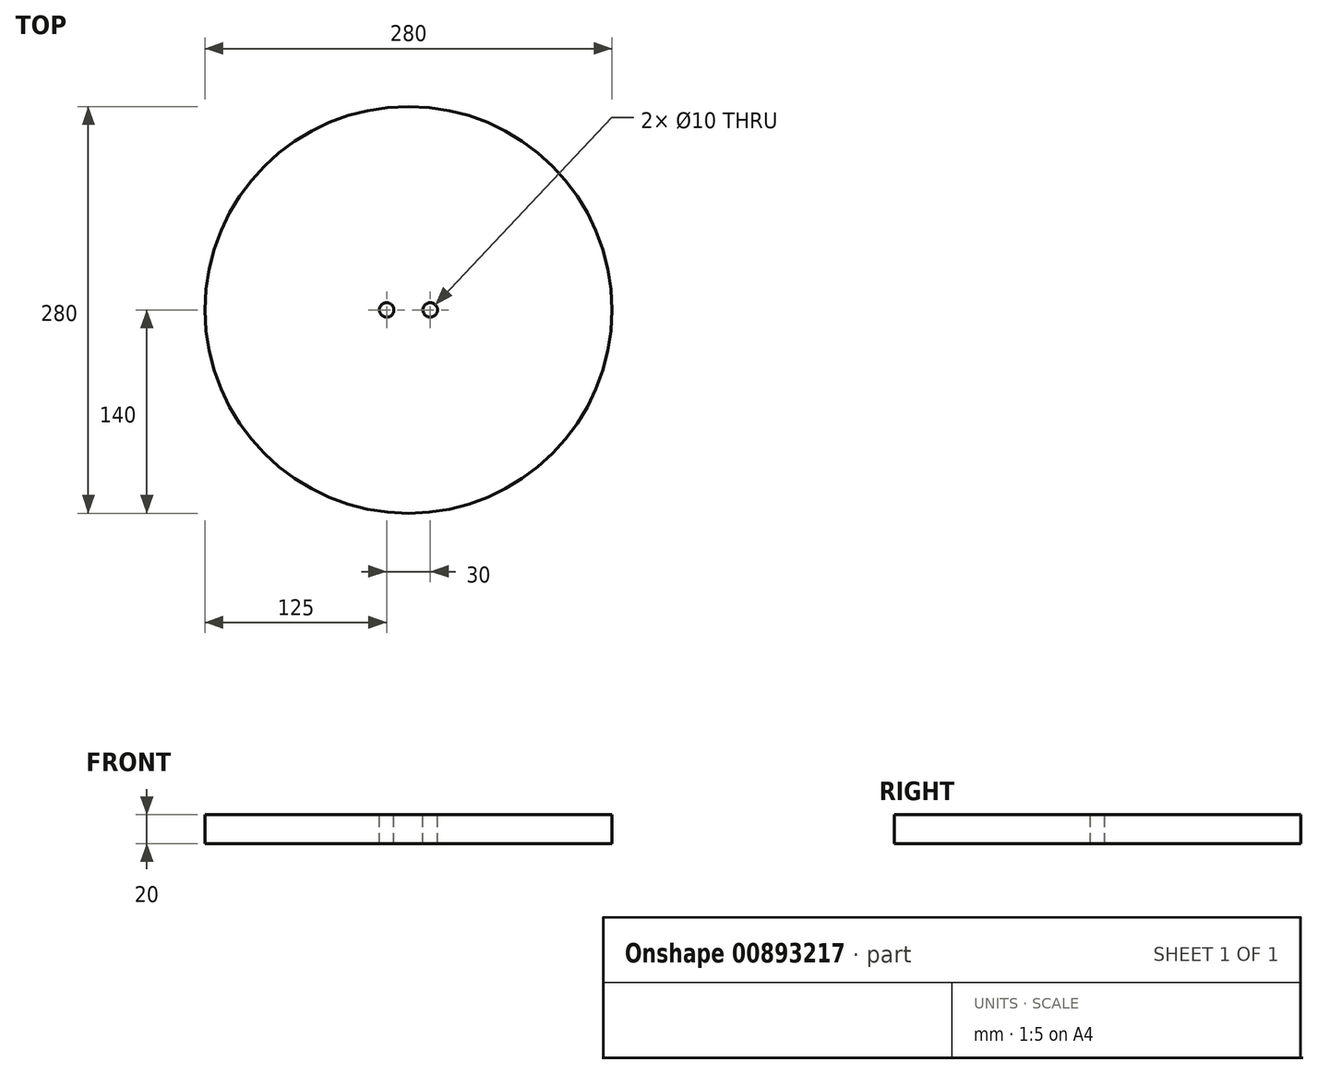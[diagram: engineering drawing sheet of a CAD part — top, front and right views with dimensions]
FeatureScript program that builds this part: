
annotation { "Feature Type Name" : "Feature", "Feature Type Description" : "" }
export const myFeature = defineFeature(function(context is Context, id is Id, definition is map)
    precondition{}
    {
        {
            var Q0;
            Q0=qCreatedBy(makeId("Top.planeOp"),FACE);
            var sketch = newSketch(context, id + "F0", { "sketchPlane" : qUnion([Q0])});
            skCircle(sketch, "E0", {"center": v(0, 0) * mm, "radius": 140 * mm});
            skSolve(sketch);
        }
        {
            var Q0;
            Q0 = qSketchRegion(id + "F0", true);
            extrude(context, id + "F1", {"entities" : qUnion([Q0]), "depth" : 20 * mm, "offsetDistance" : 25 * mm});
        }
        {
            var Q0;
            Q0=makeQuery(id+"F1.opExtrude","CAP_FACE",FACE,{"disambiguationData":[OSD([sQuery(id+"F0.wireOp",EDGE,"E0")])],"isStart":false});
            var sketch = newSketch(context, id + "F2", { "sketchPlane" : qUnion([Q0])});
            skCircle(sketch, "E1", {"center": v(-15, 0) * mm, "radius": 5 * mm});
            skCircle(sketch, "E2", {"center": v(15, 0) * mm, "radius": 5 * mm});
            skSolve(sketch);
        }
        {
            var Q0;
            Q0=makeQuery(id+"F2.imprint","IMPRINT",FACE,{"disambiguationData":[TD([[makeQuery(id+"F2.imprint","IMPRINT",EDGE,{"derivedFrom":sQuery(id+"F2.wireOp",EDGE,"E2")}),1.0]])]});
            var Q1;
            Q1=makeQuery(id+"F2.imprint","IMPRINT",FACE,{"disambiguationData":[TD([[makeQuery(id+"F2.imprint","IMPRINT",EDGE,{"derivedFrom":sQuery(id+"F2.wireOp",EDGE,"E1")}),1.0]])]});
            extrude(context, id + "F3", {"entities" : qUnion([Q0, Q1]), "operationType" : NewBodyOperationType.REMOVE, "endBound" : BoundingType.THROUGH_ALL, "oppositeDirection" : true, "depth" : 25 * mm, "offsetDistance" : 25 * mm});
        }
    });
